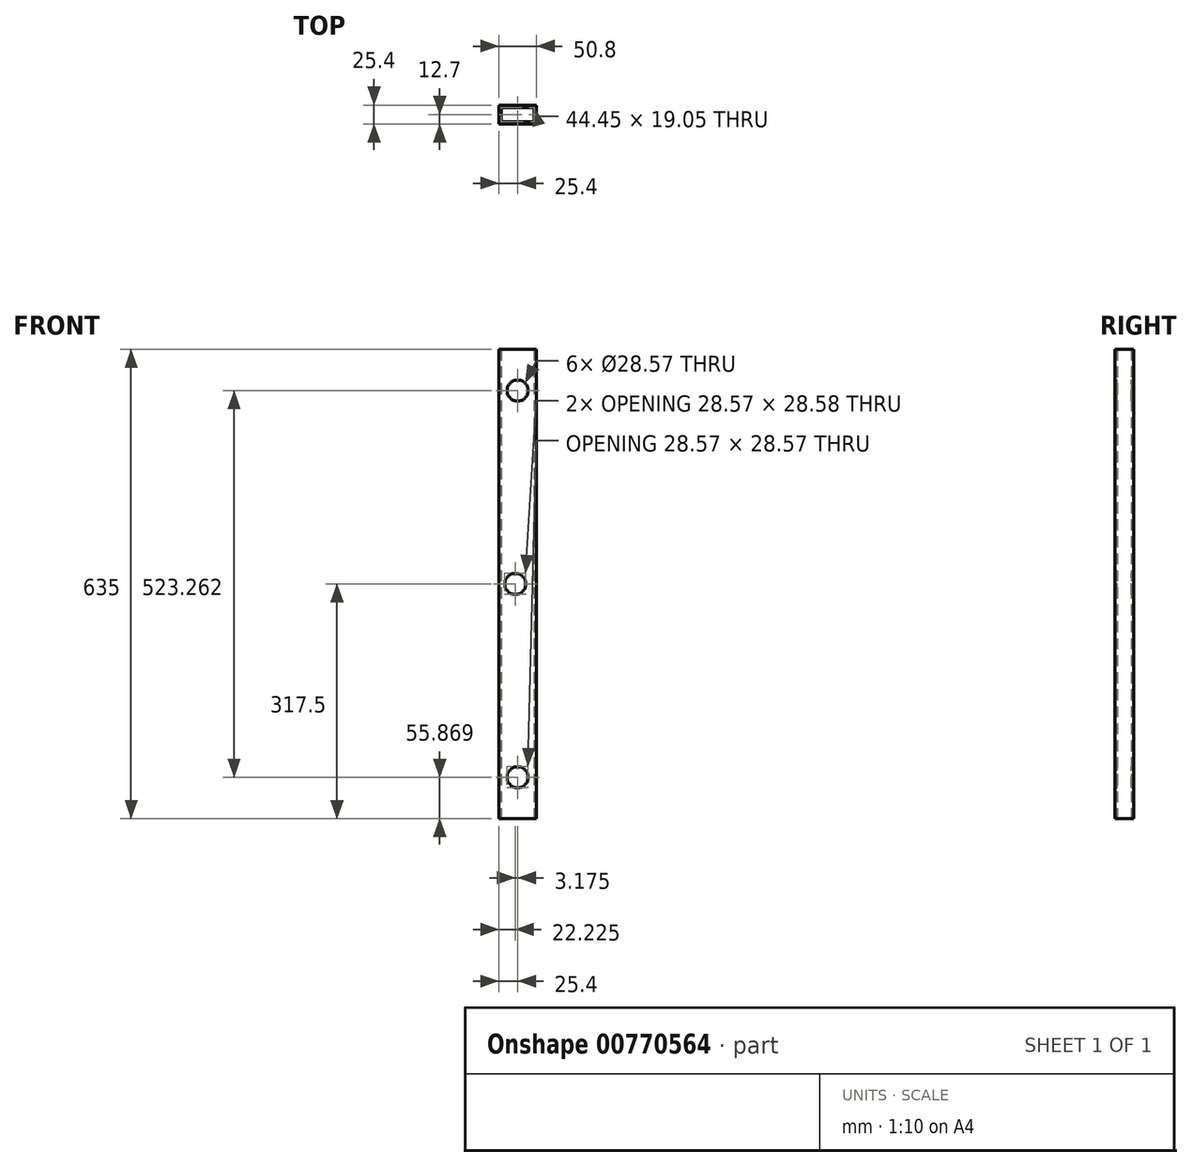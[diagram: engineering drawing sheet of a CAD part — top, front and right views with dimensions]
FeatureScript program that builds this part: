
annotation { "Feature Type Name" : "Feature", "Feature Type Description" : "" }
export const myFeature = defineFeature(function(context is Context, id is Id, definition is map)
    precondition{}
    {
        {
            var Q0;
            Q0=qCreatedBy(makeId("Top.planeOp"),FACE);
            var sketch = newSketch(context, id + "F0", { "sketchPlane" : qUnion([Q0])});
            skLineSegment(sketch, "E0", {"start": v(0, 0) * mm, "end": v(-50.8, 0) * mm});
            skLineSegment(sketch, "E1", {"start": v(-50.8, 0) * mm, "end": v(-50.8, -25.4) * mm});
            skLineSegment(sketch, "E2", {"start": v(-50.8, -25.4) * mm, "end": v(0, -25.4) * mm});
            skLineSegment(sketch, "E3", {"start": v(0, -25.4) * mm, "end": v(0, 0) * mm});
            skLineSegment(sketch, "E4.bottom", {"start": v(-3.18, -22.23) * mm, "end": v(-47.63, -22.23) * mm});
            skLineSegment(sketch, "E4.top", {"start": v(-3.18, -3.18) * mm, "end": v(-47.63, -3.18) * mm});
            skLineSegment(sketch, "E4.left", {"start": v(-3.18, -22.23) * mm, "end": v(-3.18, -3.17) * mm});
            skLineSegment(sketch, "E4.right", {"start": v(-47.63, -22.23) * mm, "end": v(-47.63, -3.18) * mm});
            skPoint(sketch, "E4.middle", {"position": v(-25.4, -12.7) * mm});
            skPoint(sketch, "E5.endSnap0", {"position": v(-25.4, -3.18) * mm});
            skLineSegment(sketch, "E6", {"start": v(-25.4, 0) * mm, "end": v(-25.4, -3.18) * mm, "construction": true});
            skLineSegment(sketch, "E7", {"start": v(-50.8, -12.7) * mm, "end": v(-47.63, -12.7) * mm, "construction": true});
            skSolve(sketch);
        }
        {
            var Q0;
            Q0 = qSketchRegion(id + "F0", true);
            extrude(context, id + "F1", {"entities" : qUnion([Q0]), "depth" : 635 * mm, "offsetDistance" : 25.4 * mm});
        }
        {
            var Q0;
            Q0=makeQuery(id+"F1.opExtrude","SWEPT_FACE",FACE,{"disambiguationData":[OSD([sQuery(id+"F0.wireOp",EDGE,"E0")])]});
            var sketch = newSketch(context, id + "F2", { "sketchPlane" : qUnion([Q0])});
            skLineSegment(sketch, "E8", {"start": v(25.4, 55.87) * mm, "end": v(28.58, 317.5) * mm, "construction": true});
            skLineSegment(sketch, "E9", {"start": v(28.58, 317.5) * mm, "end": v(25.4, 579.13) * mm, "construction": true});
            skLineSegment(sketch, "E10", {"start": v(25.4, 579.13) * mm, "end": v(25.4, 55.87) * mm, "construction": true});
            skLineSegment(sketch, "E11", {"start": v(25.4, 317.5) * mm, "end": v(0, 317.5) * mm, "construction": true});
            skCircle(sketch, "E12", {"center": v(25.4, 55.87) * mm, "radius": 14.29 * mm});
            skCircle(sketch, "E13", {"center": v(25.4, 579.13) * mm, "radius": 14.29 * mm});
            skCircle(sketch, "E14", {"center": v(28.58, 317.5) * mm, "radius": 14.29 * mm});
            skSolve(sketch);
        }
        {
            var Q0;
            Q0 = qSketchRegion(id + "F2", true);
            extrude(context, id + "F3", {"entities" : qUnion([Q0]), "operationType" : NewBodyOperationType.REMOVE, "endBound" : BoundingType.THROUGH_ALL, "oppositeDirection" : true, "depth" : 25.4 * mm, "offsetDistance" : 25.4 * mm});
        }
    });
